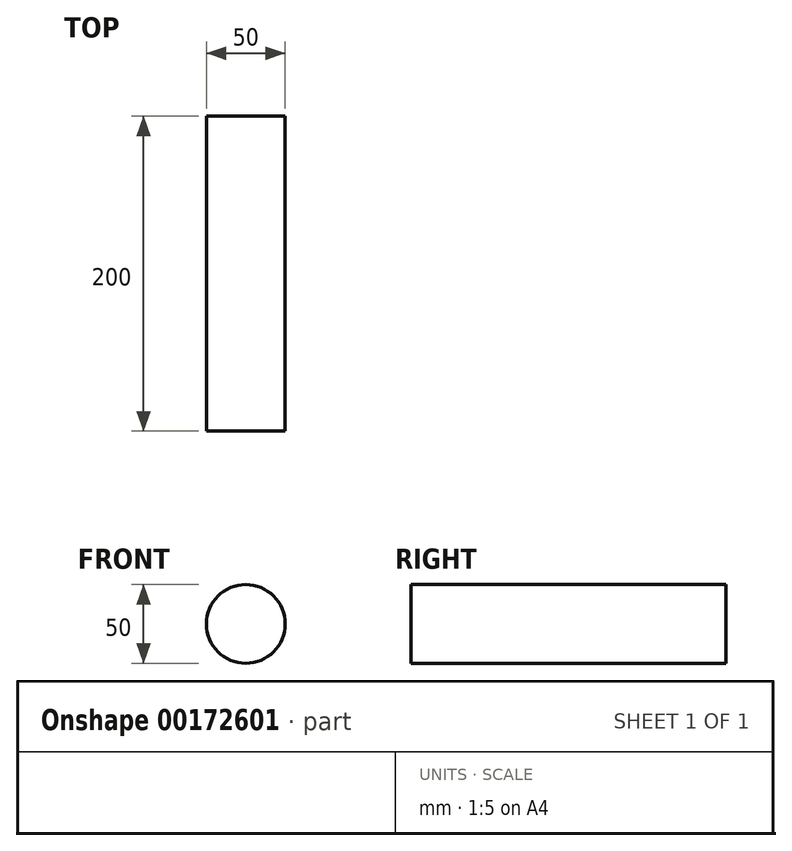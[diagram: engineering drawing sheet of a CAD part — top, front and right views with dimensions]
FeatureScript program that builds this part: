
annotation { "Feature Type Name" : "Feature", "Feature Type Description" : "" }
export const myFeature = defineFeature(function(context is Context, id is Id, definition is map)
    precondition{}
    {
        {
            var Q0;
            Q0=qCreatedBy(makeId("Front.planeOp"),FACE);
            var sketch = newSketch(context, id + "F0", { "sketchPlane" : qUnion([Q0])});
            skCircle(sketch, "E0", {"center": v(0, 0) * mm, "radius": 25 * mm});
            skSolve(sketch);
        }
        {
            var Q0;
            Q0 = qSketchRegion(id + "F0", true);
            extrude(context, id + "F1", {"entities" : qUnion([Q0]), "endBound" : BoundingType.SYMMETRIC, "depth" : 200 * mm});
        }
    });
